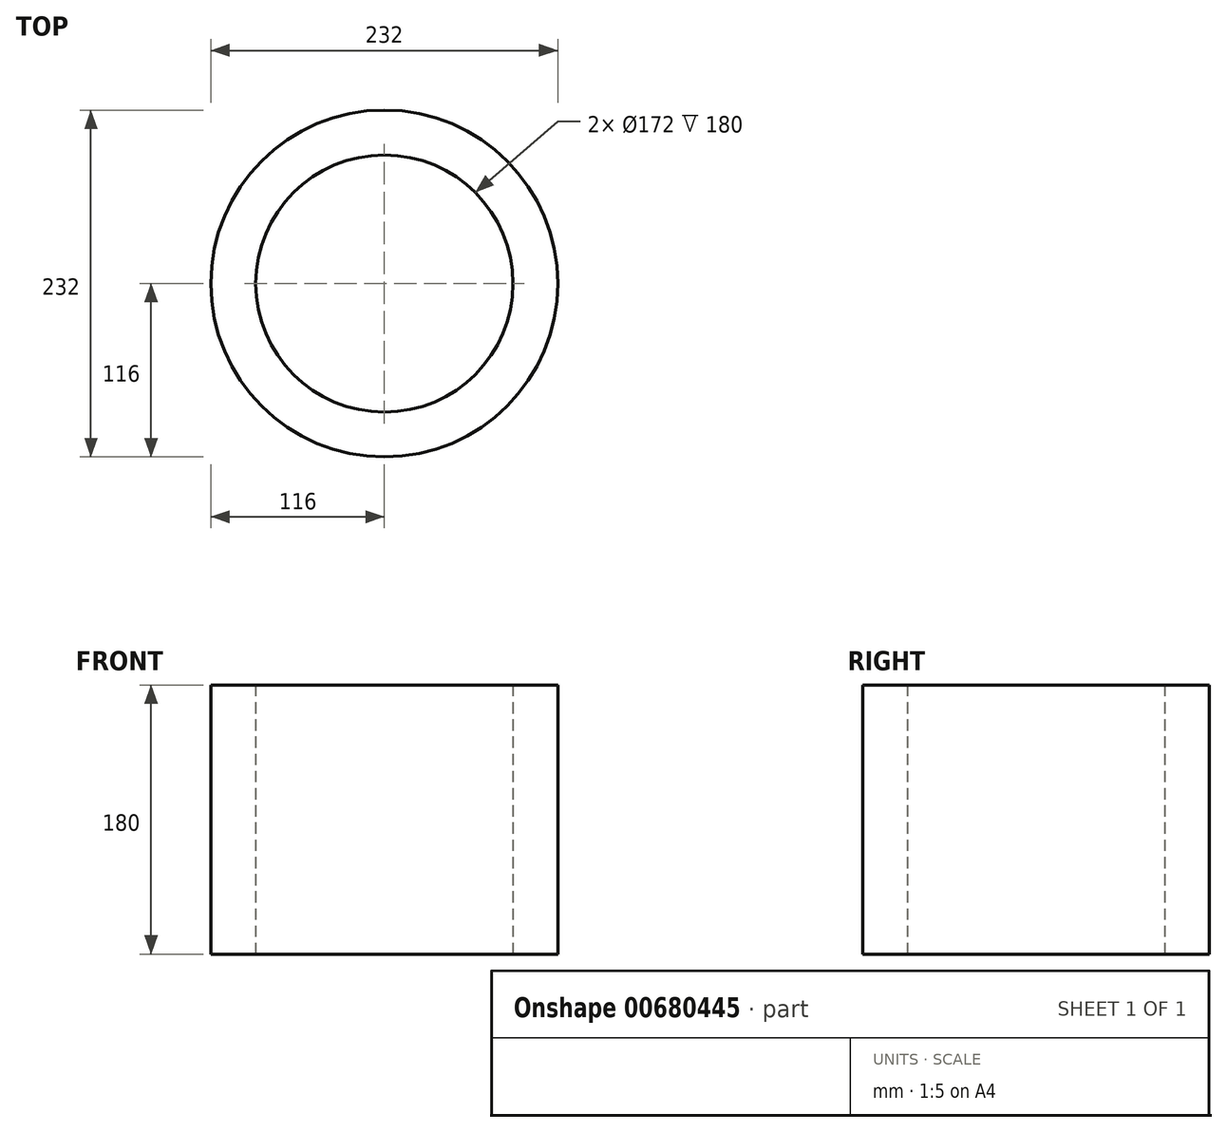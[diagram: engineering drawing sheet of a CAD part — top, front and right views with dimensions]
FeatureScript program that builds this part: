
annotation { "Feature Type Name" : "Feature", "Feature Type Description" : "" }
export const myFeature = defineFeature(function(context is Context, id is Id, definition is map)
    precondition{}
    {
        {
            var Q0;
            Q0=qCreatedBy(makeId("Top.planeOp"),FACE);
            var sketch = newSketch(context, id + "F0", { "sketchPlane" : qUnion([Q0])});
            skCircle(sketch, "E0", {"center": v(0, 0) * mm, "radius": 116 * mm});
            skCircle(sketch, "E1", {"center": v(0, 0) * mm, "radius": 86 * mm});
            skSolve(sketch);
        }
        {
            var Q0;
            Q0=makeQuery(id+"F0.imprint","IMPRINT",FACE,{"disambiguationData":[TD([[makeQuery(id+"F0.imprint","IMPRINT",EDGE,{"derivedFrom":sQuery(id+"F0.wireOp",EDGE,"E0")}),1.0]])]});
            extrude(context, id + "F1", {"entities" : qUnion([Q0]), "depth" : 180 * mm, "offsetDistance" : 25.4 * mm});
        }
    });
